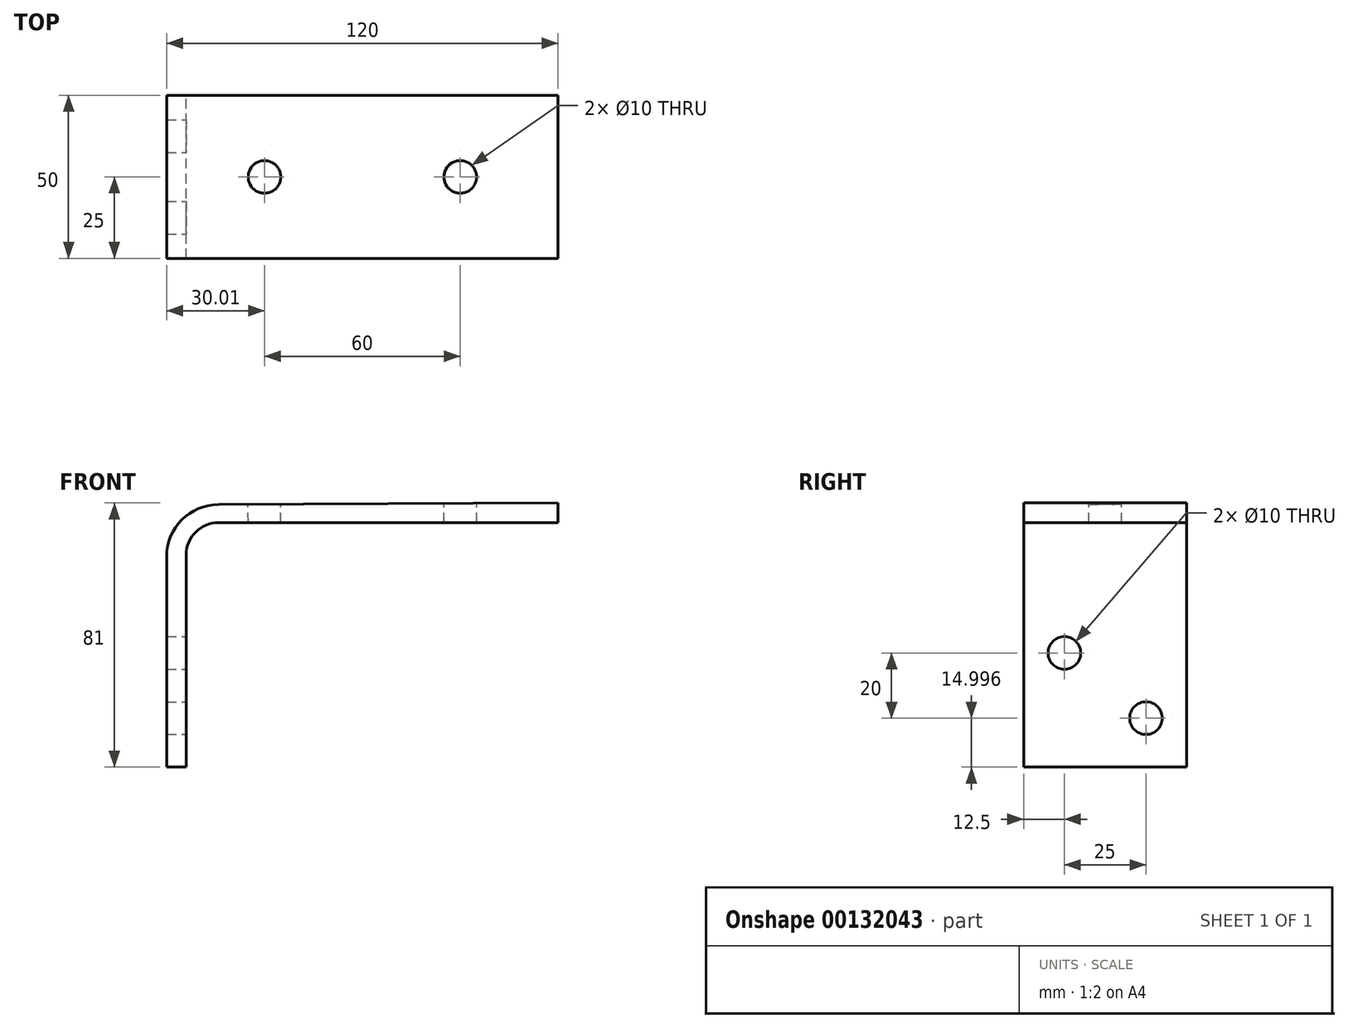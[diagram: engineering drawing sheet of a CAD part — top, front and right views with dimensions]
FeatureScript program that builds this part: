
annotation { "Feature Type Name" : "Feature", "Feature Type Description" : "" }
export const myFeature = defineFeature(function(context is Context, id is Id, definition is map)
    precondition{}
    {
        {
            var Q0;
            Q0=qCreatedBy(makeId("Front.planeOp"),FACE);
            var sketch = newSketch(context, id + "F0", { "sketchPlane" : qUnion([Q0])});
            skLineSegment(sketch, "E0", {"start": v(-59.8, 56) * mm, "end": v(-59.8, -8.52) * mm});
            skLineSegment(sketch, "E1", {"start": v(-59.8, -8.52) * mm, "end": v(-53.8, -8.52) * mm});
            skLineSegment(sketch, "E2", {"start": v(-53.8, -8.52) * mm, "end": v(-53.8, 56.48) * mm});
            skLineSegment(sketch, "E3", {"start": v(-43.8, 66.48) * mm, "end": v(60.2, 66.48) * mm});
            skLineSegment(sketch, "E4", {"start": v(60.2, 66.48) * mm, "end": v(60.2, 72.48) * mm});
            skLineSegment(sketch, "E5", {"start": v(60.2, 72.48) * mm, "end": v(-43.88, 72) * mm});
            skPoint(sketch, "E6.visualSharp", {"position": v(-53.8, 66.48) * mm});
            skArc(sketch, "E6.filletArc", {"start": v(-43.8, 66.48) * mm, "mid": v(-50.87, 63.55) * mm, "end": v(-53.8, 56.48) * mm});
            skPoint(sketch, "E7.visualSharp", {"position": v(-59.8, 71.92) * mm});
            skArc(sketch, "E7.filletArc", {"start": v(-43.88, 72) * mm, "mid": v(-55.14, 67.28) * mm, "end": v(-59.8, 56) * mm});
            skSolve(sketch);
        }
        {
            var Q0;
            Q0 = qSketchRegion(id + "F0", true);
            extrude(context, id + "F1", {"entities" : qUnion([Q0]), "depth" : 50 * mm});
        }
        {
            var Q0;
            Q0=makeQuery(id+"F1.opExtrude","SWEPT_FACE",FACE,{"disambiguationData":[OSD([sQuery(id+"F0.wireOp",EDGE,"E5")])]});
            var sketch = newSketch(context, id + "F2", { "sketchPlane" : qUnion([Q0])});
            skCircle(sketch, "E8", {"center": v(-29.47, -25) * mm, "radius": 5 * mm});
            skCircle(sketch, "E9", {"center": v(30.53, -25) * mm, "radius": 5 * mm});
            skSolve(sketch);
        }
        {
            var Q0;
            Q0 = qSketchRegion(id + "F2", true);
            extrude(context, id + "F3", {"entities" : qUnion([Q0]), "operationType" : NewBodyOperationType.REMOVE, "oppositeDirection" : true, "depth" : 25 * mm});
        }
        {
            var Q0;
            Q0=makeQuery(id+"F1.opExtrude","SWEPT_FACE",FACE,{"disambiguationData":[OSD([sQuery(id+"F0.wireOp",EDGE,"E2")])]});
            var sketch = newSketch(context, id + "F4", { "sketchPlane" : qUnion([Q0])});
            skCircle(sketch, "E10", {"center": v(-12.5, 6.48) * mm, "radius": 5 * mm});
            skCircle(sketch, "E11", {"center": v(-37.5, 26.48) * mm, "radius": 5 * mm});
            skSolve(sketch);
        }
        {
            var Q0;
            Q0 = qSketchRegion(id + "F4", true);
            extrude(context, id + "F5", {"entities" : qUnion([Q0]), "operationType" : NewBodyOperationType.REMOVE, "oppositeDirection" : true, "depth" : 25 * mm});
        }
    });
